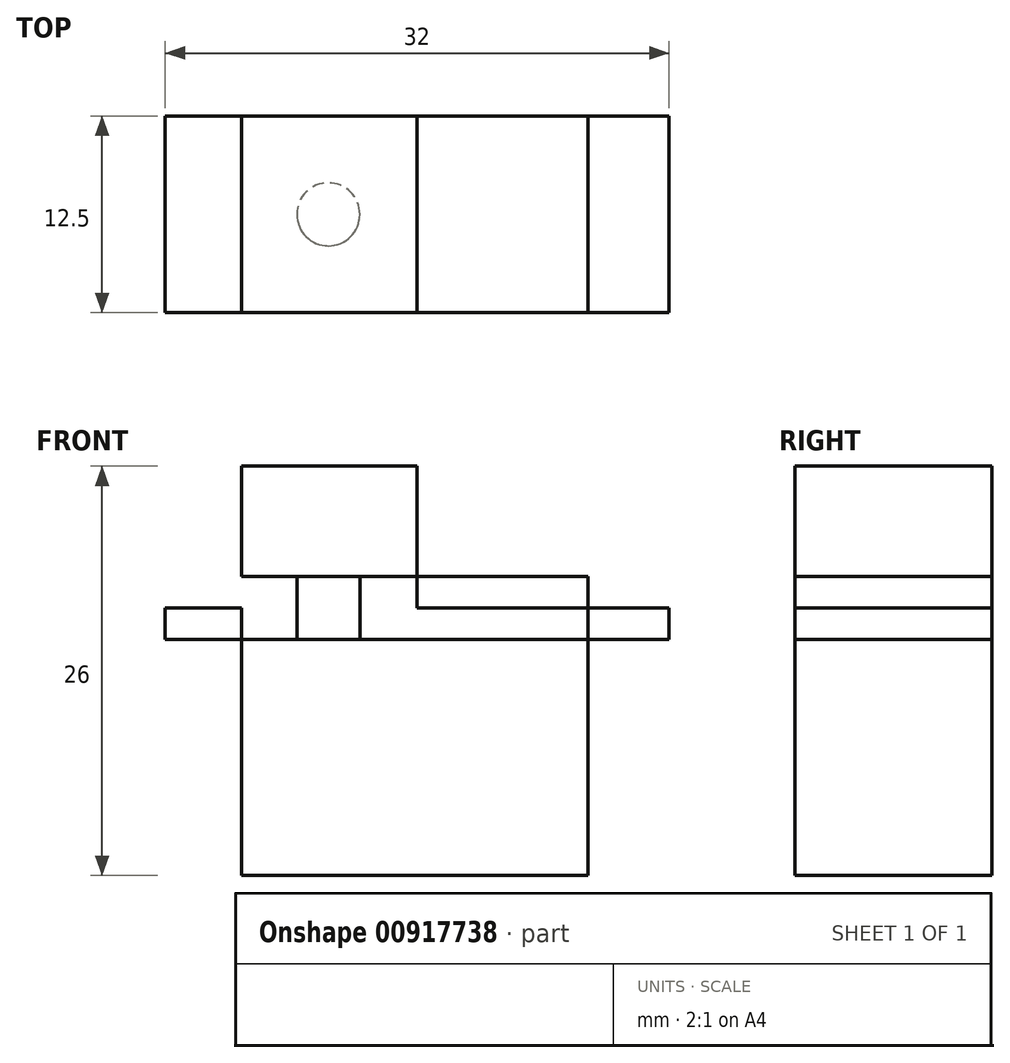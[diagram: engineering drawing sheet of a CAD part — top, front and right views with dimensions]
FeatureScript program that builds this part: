
annotation { "Feature Type Name" : "Feature", "Feature Type Description" : "" }
export const myFeature = defineFeature(function(context is Context, id is Id, definition is map)
    precondition{}
    {
        {
            var Q0;
            Q0=qCreatedBy(makeId("Front.planeOp"),FACE);
            var sketch = newSketch(context, id + "F0", { "sketchPlane" : qUnion([Q0])});
            skLineSegment(sketch, "E0.bottom", {"start": v(-11.14, 0) * mm, "end": v(10.86, 0) * mm});
            skLineSegment(sketch, "E0.top", {"start": v(-11.14, 29.5) * mm, "end": v(10.86, 29.5) * mm});
            skLineSegment(sketch, "E0.left", {"start": v(-11.14, 0) * mm, "end": v(-11.14, 29.5) * mm});
            skLineSegment(sketch, "E0.right", {"start": v(10.86, 0) * mm, "end": v(10.86, 29.5) * mm});
            skLineSegment(sketch, "E1.bottom", {"start": v(-16, 17) * mm, "end": v(16, 17) * mm});
            skLineSegment(sketch, "E1.top", {"start": v(-16, 15) * mm, "end": v(16, 15) * mm});
            skLineSegment(sketch, "E1.left", {"start": v(-16, 17) * mm, "end": v(-16, 15) * mm});
            skLineSegment(sketch, "E1.right", {"start": v(16, 17) * mm, "end": v(16, 15) * mm});
            skLineSegment(sketch, "E2", {"start": v(0, 29.5) * mm, "end": v(0, 0) * mm});
            skLineSegment(sketch, "E3", {"start": v(0, 17) * mm, "end": v(0, 15) * mm});
            skLineSegment(sketch, "E4", {"start": v(-11.14, 19) * mm, "end": v(10.86, 19) * mm});
            skLineSegment(sketch, "E5.bottom", {"start": v(-11.14, 26) * mm, "end": v(0, 26) * mm});
            skLineSegment(sketch, "E5.top", {"start": v(-11.14, 17) * mm, "end": v(0, 17) * mm});
            skLineSegment(sketch, "E5.left", {"start": v(-11.14, 26) * mm, "end": v(-11.14, 17) * mm});
            skLineSegment(sketch, "E5.right", {"start": v(0, 26) * mm, "end": v(0, 17) * mm});
            skSolve(sketch);
        }
        {
            var Q0;
            {var subQ0=sQuery(id+"F0.wireOp",EDGE,"E0.left");var subQ1=sQuery(id+"F0.wireOp",EDGE,"E0.bottom");var subQ2=makeQuery(id+"F0.imprint","INTERSECT",VERTEX,{"derivedFrom":[subQ1,subQ0]});Q0=makeQuery(id+"F0.imprint","IMPRINT",FACE,{"disambiguationData":[TD([[makeQuery(id+"F0.imprint","IMPRINT",EDGE,{"disambiguationData":[TD([[subQ2,-1.0]])],"derivedFrom":subQ1}),1.0]])]});}
            var Q1;
            {var subQ5=sQuery(id+"F0.wireOp",EDGE,"E3");Q1=makeQuery(id+"F0.imprint","IMPRINT",FACE,{"disambiguationData":[TD([[makeQuery(id+"F0.imprint","IMPRINT",EDGE,{"derivedFrom":subQ5}),1.0]])]});}
            var Q2;
            {var subQ4=sQuery(id+"F0.wireOp",EDGE,"E3");Q2=makeQuery(id+"F0.imprint","IMPRINT",FACE,{"disambiguationData":[TD([[makeQuery(id+"F0.imprint","IMPRINT",EDGE,{"derivedFrom":subQ4}),-1.0]])]});}
            var Q3;
            {var subQ5=sQuery(id+"F0.wireOp",EDGE,"E1.left");Q3=makeQuery(id+"F0.imprint","IMPRINT",FACE,{"disambiguationData":[TD([[makeQuery(id+"F0.imprint","IMPRINT",EDGE,{"derivedFrom":subQ5}),1.0]])]});}
            var Q4;
            {var subQ0=sQuery(id+"F0.wireOp",EDGE,"E0.right");var subQ1=sQuery(id+"F0.wireOp",EDGE,"E0.bottom");var subQ2=makeQuery(id+"F0.imprint","INTERSECT",VERTEX,{"derivedFrom":[subQ1,subQ0]});Q4=makeQuery(id+"F0.imprint","IMPRINT",FACE,{"disambiguationData":[TD([[makeQuery(id+"F0.imprint","IMPRINT",EDGE,{"disambiguationData":[TD([[subQ2,1.0]])],"derivedFrom":subQ1}),1.0]])]});}
            var Q5;
            {var subQ5=sQuery(id+"F0.wireOp",EDGE,"E1.right");Q5=makeQuery(id+"F0.imprint","IMPRINT",FACE,{"disambiguationData":[TD([[makeQuery(id+"F0.imprint","IMPRINT",EDGE,{"derivedFrom":subQ5}),-1.0]])]});}
            var Q6;
            {var subQ0=sQuery(id+"F0.wireOp",EDGE,"E4");var subQ1=sQuery(id+"F0.wireOp",EDGE,"E0.right");var subQ2=makeQuery(id+"F0.imprint","INTERSECT",VERTEX,{"derivedFrom":[subQ1,subQ0]});Q6=makeQuery(id+"F0.imprint","IMPRINT",FACE,{"disambiguationData":[TD([[makeQuery(id+"F0.imprint","IMPRINT",EDGE,{"disambiguationData":[TD([[subQ2,1.0]])],"derivedFrom":subQ1}),1.0]])]});}
            var Q7;
            {var subQ5=sQuery(id+"F0.wireOp",EDGE,"E5.bottom");Q7=makeQuery(id+"F0.imprint","IMPRINT",FACE,{"disambiguationData":[TD([[makeQuery(id+"F0.imprint","IMPRINT",EDGE,{"derivedFrom":subQ5}),-1.0]])]});}
            var Q8;
            {var subQ5=sQuery(id+"F0.wireOp",EDGE,"E5.top");Q8=makeQuery(id+"F0.imprint","IMPRINT",FACE,{"disambiguationData":[TD([[makeQuery(id+"F0.imprint","IMPRINT",EDGE,{"derivedFrom":subQ5}),1.0]])]});}
            extrude(context, id + "F1", {"entities" : qUnion([Q0, Q1, Q2, Q3, Q4, Q5, Q6, Q7, Q8]), "depth" : 12.5 * mm, "offsetDistance" : 25 * mm, "symmetric" : true});
        }
        {
            var Q0;
            Q0=makeQuery(id+"F1.opExtrude","SWEPT_FACE",FACE,{"disambiguationData":[OSD([sQuery(id+"F0.wireOp",EDGE,"E4")])]});
            var sketch = newSketch(context, id + "F2", { "sketchPlane" : qUnion([Q0])});
            skCircle(sketch, "E6", {"center": v(-5.64, 0) * mm, "radius": 2 * mm});
            skSolve(sketch);
        }
        {
            var Q0;
            Q0=makeQuery(id+"F2.imprint","IMPRINT",FACE,{"disambiguationData":[TD([[makeQuery(id+"F2.imprint","IMPRINT",EDGE,{"derivedFrom":sQuery(id+"F2.wireOp",EDGE,"E6")}),1.0]])]});
            extrude(context, id + "F3", {"entities" : qUnion([Q0]), "operationType" : NewBodyOperationType.ADD, "depth" : 11 * mm, "offsetDistance" : 25 * mm});
        }
    });
